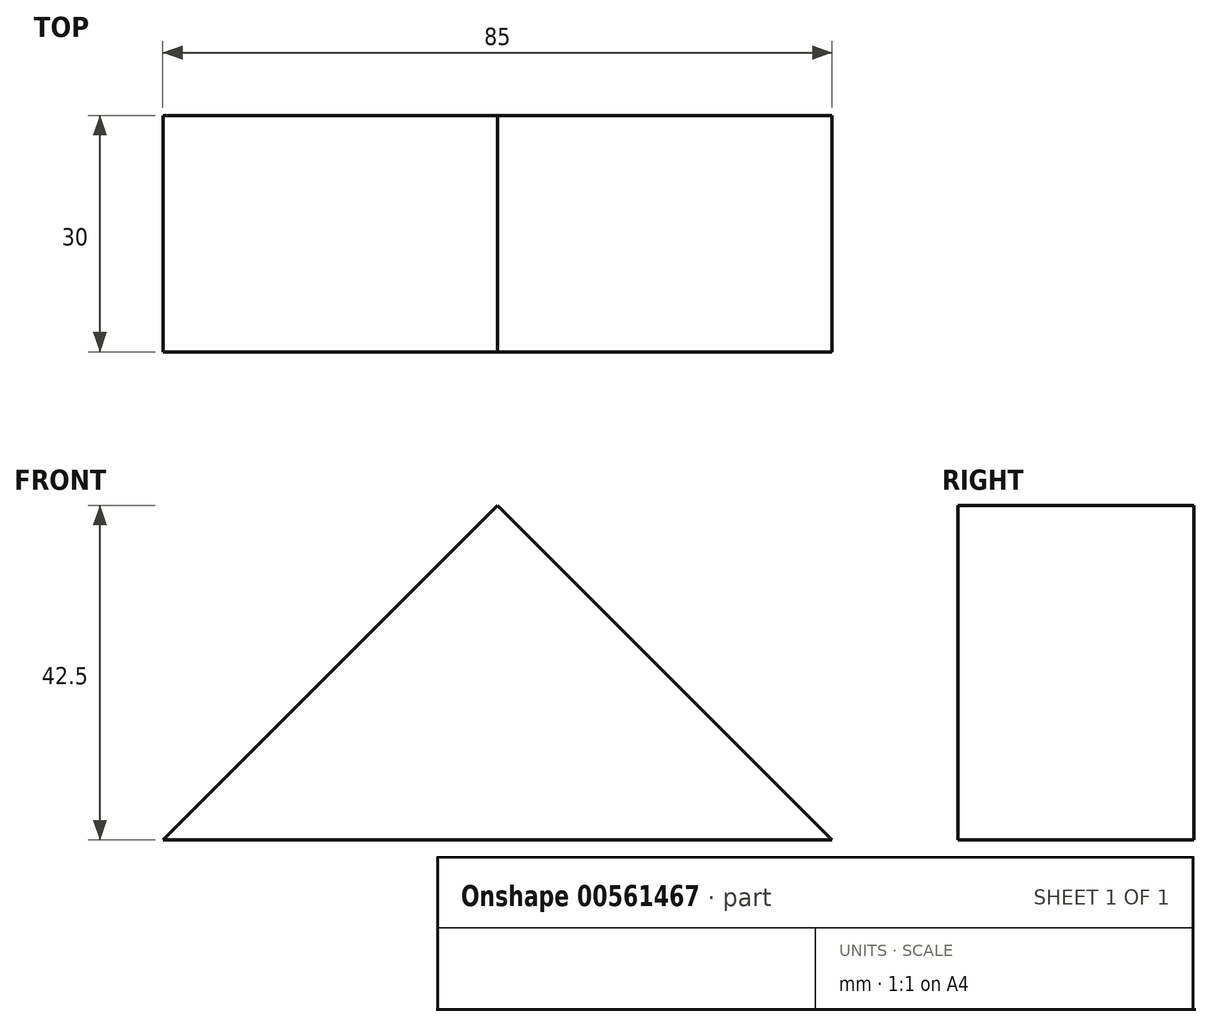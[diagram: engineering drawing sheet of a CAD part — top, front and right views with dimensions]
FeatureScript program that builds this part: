
annotation { "Feature Type Name" : "Feature", "Feature Type Description" : "" }
export const myFeature = defineFeature(function(context is Context, id is Id, definition is map)
    precondition{}
    {
        {
            var Q0;
            Q0=qCreatedBy(makeId("Front.planeOp"),FACE);
            var sketch = newSketch(context, id + "F0", { "sketchPlane" : qUnion([Q0])});
            skLineSegment(sketch, "E0", {"start": v(-43.08, -40.39) * mm, "end": v(41.92, -40.39) * mm});
            skLineSegment(sketch, "E1", {"start": v(41.92, -40.39) * mm, "end": v(-0.58, 2.11) * mm});
            skLineSegment(sketch, "E2", {"start": v(-0.58, 2.11) * mm, "end": v(-43.08, -40.39) * mm});
            skSolve(sketch);
        }
        {
            var Q0;
            Q0 = qSketchRegion(id + "F0", true);
            extrude(context, id + "F1", {"entities" : qUnion([Q0]), "depth" : 30 * mm, "offsetDistance" : 25 * mm});
        }
    });
